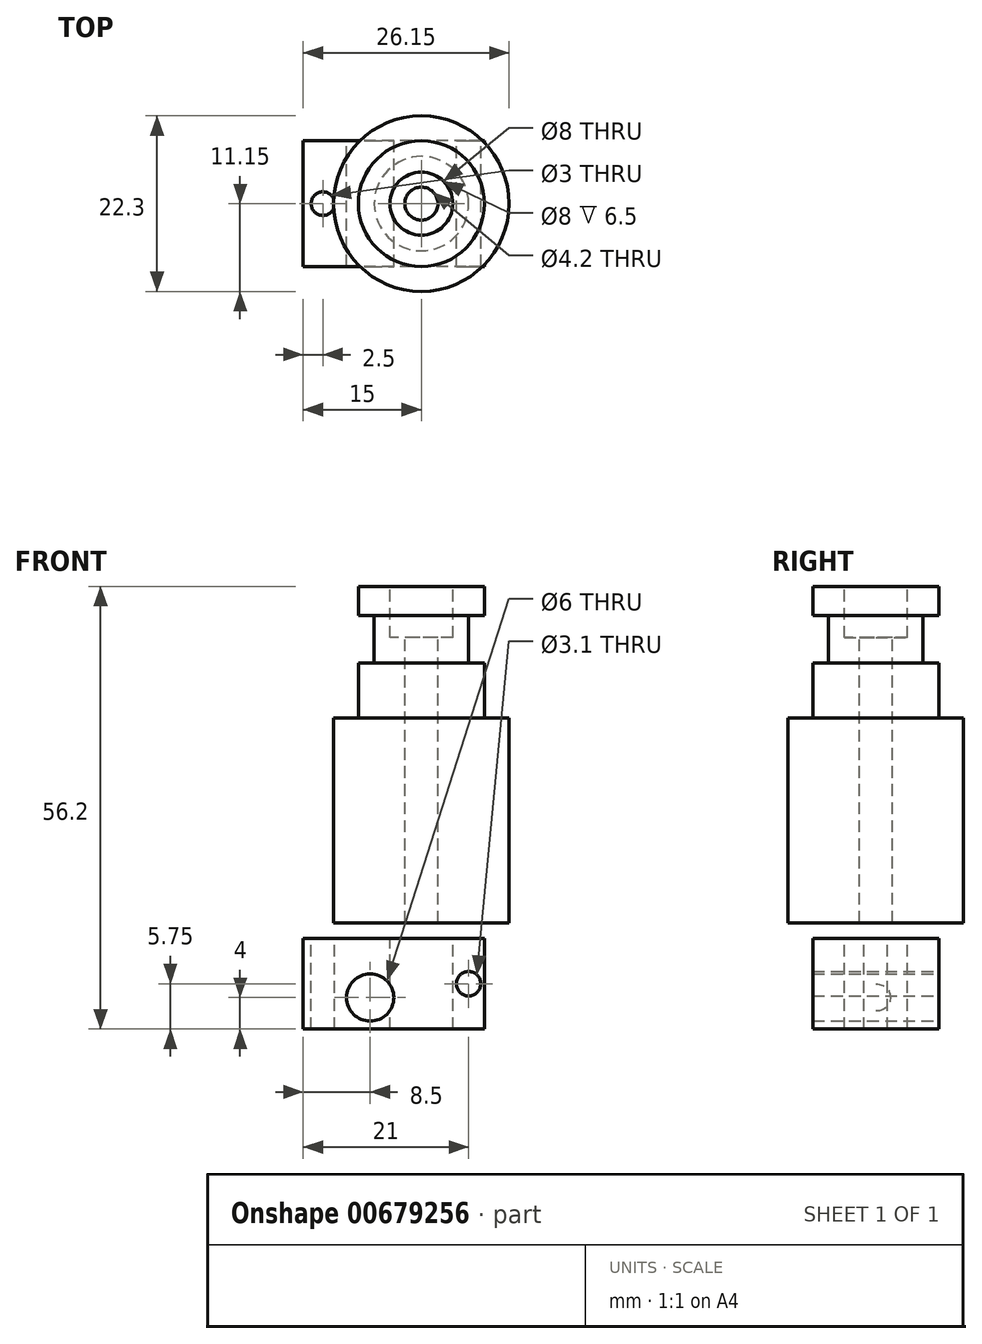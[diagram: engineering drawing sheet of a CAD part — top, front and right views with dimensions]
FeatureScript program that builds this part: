
annotation { "Feature Type Name" : "Feature", "Feature Type Description" : "" }
export const myFeature = defineFeature(function(context is Context, id is Id, definition is map)
    precondition{}
    {
        {
            var Q0;
            Q0=qCreatedBy(makeId("Front.planeOp"),FACE);
            var sketch = newSketch(context, id + "F0", { "sketchPlane" : qUnion([Q0])});
            skLineSegment(sketch, "E0", {"start": v(0, 0) * mm, "end": v(0, -28) * mm, "construction": true});
            skLineSegment(sketch, "E1.0", {"start": v(2.1, -6.5) * mm, "end": v(2.1, -42.7) * mm});
            skLineSegment(sketch, "E2", {"start": v(8, 0) * mm, "end": v(8, -3.7) * mm});
            skLineSegment(sketch, "E3", {"start": v(8, -3.7) * mm, "end": v(6, -3.7) * mm});
            skLineSegment(sketch, "E4", {"start": v(6, -3.7) * mm, "end": v(6, -9.7) * mm});
            skLineSegment(sketch, "E5", {"start": v(6, -9.7) * mm, "end": v(8, -9.7) * mm});
            skLineSegment(sketch, "E6", {"start": v(8, -9.7) * mm, "end": v(8, -16.7) * mm});
            skLineSegment(sketch, "E7", {"start": v(4, 0) * mm, "end": v(8, 0) * mm});
            skLineSegment(sketch, "E8", {"start": v(0, 0) * mm, "end": v(2.1, 0) * mm, "construction": true});
            skLineSegment(sketch, "E9", {"start": v(4, 0) * mm, "end": v(4, -6.5) * mm});
            skLineSegment(sketch, "E10", {"start": v(4, -6.5) * mm, "end": v(2.1, -6.5) * mm});
            skLineSegment(sketch, "E11", {"start": v(8, -16.7) * mm, "end": v(11.15, -16.7) * mm});
            skLineSegment(sketch, "E12", {"start": v(11.15, -16.7) * mm, "end": v(11.15, -42.7) * mm});
            skLineSegment(sketch, "E13", {"start": v(11.15, -42.7) * mm, "end": v(2.1, -42.7) * mm});
            skSolve(sketch);
        }
        {
            var Q0;
            Q0=makeQuery(id+"F0.imprint","IMPRINT",FACE,{"disambiguationData":[TD([[makeQuery(id+"F0.imprint","IMPRINT",EDGE,{"derivedFrom":sQuery(id+"F0.wireOp",EDGE,"E1.0")}),1.0]])]});
            var Q1;
            Q1=sQuery(id+"F0.wireOp",EDGE,"E0");
            revolve(context, id + "F1", {"entities" : qUnion([Q0]), "axis" : qUnion([Q1]), "revolveType" : RevolveType.FULL});
        }
        {
            var Q0;
            Q0=makeQuery(id+"F1.opRevolve","SWEPT_FACE",FACE,{"disambiguationData":[OSD([sQuery(id+"F0.wireOp",EDGE,"E13")])]});
            cPlane(context, id + "F2", {"entities" : qUnion([Q0]), "cplaneType" : CPlaneType.OFFSET, "offset" : 2 * mm, "width" : 150 * mm, "height" : 150 * mm});
        }
        {
            var Q0;
            Q0=qCreatedBy(id+"F2.planeOp",FACE);
            var sketch = newSketch(context, id + "F3", { "sketchPlane" : qUnion([Q0])});
            skPoint(sketch, "E14.0", {"position": v(0, 0) * mm});
            skLineSegment(sketch, "E15.bottom", {"start": v(11.5, -8) * mm, "end": v(-11.5, -8) * mm});
            skLineSegment(sketch, "E15.top", {"start": v(11.5, 8) * mm, "end": v(-11.5, 8) * mm});
            skLineSegment(sketch, "E15.left", {"start": v(11.5, -8) * mm, "end": v(11.5, 8) * mm});
            skLineSegment(sketch, "E15.right", {"start": v(-11.5, -8) * mm, "end": v(-11.5, 8) * mm});
            skCircle(sketch, "E16", {"center": v(3.5, 0) * mm, "radius": 4 * mm});
            skPoint(sketch, "E16.centerSnap0", {"position": v(11.5, 0) * mm});
            skCircle(sketch, "E17", {"center": v(-9, 0) * mm, "radius": 1.5 * mm});
            skSolve(sketch);
        }
        {
            var Q0;
            Q0 = qSketchRegion(id + "F3", true);
            extrude(context, id + "F4", {"entities" : qUnion([Q0]), "depth" : 11.5 * mm, "offsetDistance" : 25 * mm});
        }
        {
            var Q0;
            Q0=makeQuery(id+"F4.opExtrude","SWEPT_FACE",FACE,{"disambiguationData":[OSD([sQuery(id+"F3.wireOp",EDGE,"E15.bottom")])]});
            var sketch = newSketch(context, id + "F5", { "sketchPlane" : qUnion([Q0])});
            skCircle(sketch, "E18", {"center": v(3, -52.2) * mm, "radius": 3 * mm});
            skCircle(sketch, "E19", {"center": v(-9.5, -50.45) * mm, "radius": 1.55 * mm});
            skSolve(sketch);
        }
        {
            var Q0;
            Q0 = qSketchRegion(id + "F5", true);
            extrude(context, id + "F6", {"entities" : qUnion([Q0]), "operationType" : NewBodyOperationType.REMOVE, "endBound" : BoundingType.THROUGH_ALL, "oppositeDirection" : true, "depth" : 25 * mm, "offsetDistance" : 25 * mm});
        }
        {
            var Q0;
            Q0=makeQuery(id+"F4.opExtrude","SWEPT_BODY",BODY,{"disambiguationData":[OSD([sQuery(id+"F3.wireOp",EDGE,"E15.bottom"),sQuery(id+"F3.wireOp",EDGE,"E15.top"),sQuery(id+"F3.wireOp",EDGE,"E15.left"),sQuery(id+"F3.wireOp",EDGE,"E15.right"),sQuery(id+"F3.wireOp",EDGE,"E16"),sQuery(id+"F3.wireOp",EDGE,"E17")])]});
            transform(context, id + "F7", {"entities" : qUnion([Q0]), "transformType" : TransformType.TRANSLATION_3D, "dx" : -3.5 * mm, "dy" : 0 * mm, "dz" : 0 * mm, "makeCopy" : false});
        }
    });
